# Revit family: NLRS_27_GM_LIB_GVIP_MR
name_source: partatom
category: Generic Models
revit_build: Autodesk Revit 2017 (Build: 20190507_1515(x64)
units: mm (PartAtom-declared; Revit-internal decimal feet)

## family parameters
Can host rebar = No
Cut with Voids When Loaded = Yes
Part Type = Normal
Room Calculation Point = No
Round Connector Dimension = Use Diameter
Shared = No

## types (6) — shared parameters
01_kraal = No
02_Trim = Yes
03_druppel = Yes
Assembly Code = 27.16
Breedte_Plafond = 200 mm  [stored 0.656168 ft]
Description = GVIP Goot
IfcExportAs = IfcFlowsegment
Manufacturer = Meilof Riks bv
Model = GVIP
NLRS_C_Materiaal = RAL 9010
Type Image = <None>
URL = https://www.meilofriks.nl
Vorm_Goot_L = 01 : 2_←_Hoek_L
Vorm_Goot_L-R = 01 : 4_↔_Hoek_L-R
Vorm_Goot_R = 01 : 3_→_Hoek_R

## per-type parameters (varying)
| type | Breedte_goot | Breedte_goot_hoek | Diepte_bak | Hoogte_AK | Hoogte_VK | NLRS_C_Binnenbak | Set_Diepte_bak | set_Hoogte_AK |
| GVIP S310B | 310 mm  [stored 1.01706 ft] | 310 mm  [stored 1.01706 ft] | 76 mm  [stored 0.249344 ft] | 219 mm  [stored 0.718504 ft] | 193 mm  [stored 0.633202 ft] | RAL 7036 | 76 mm  [stored 0.249344 ft] | 219 mm  [stored 0.718504 ft] |
| GVIP S280B | 280 mm  [stored 0.918635 ft] | 280 mm  [stored 0.918635 ft] | 90 mm  [stored 0.295276 ft] | 210 mm | 182 mm | RAL 9010 | 90 mm  [stored 0.295276 ft] | 210 mm |
| GVIP S365B | 365 mm  [stored 1.19751 ft] | 365 mm  [stored 1.19751 ft] | 96 mm | 243 mm | 214 mm | RAL 9010 | 96 mm | 243 mm |
| GVIP S400B | 400 mm  [stored 1.31234 ft] | 400 mm  [stored 1.31234 ft] | 78 mm | 227 mm | 195 mm | RAL 9010 | 78 mm | 227 mm |
| GVIP S450B | 450 mm | 450 mm | 103 mm | 251 mm | 221 mm | RAL 9010 | 90 mm  [stored 0.295276 ft] | 251 mm |
| GVIP S500B | 500 mm  [stored 1.64042 ft] | 500 mm  [stored 1.64042 ft] | 78 mm | 226 mm | 196 mm  [stored 0.643045 ft] | RAL 9010 | 78 mm | 226 mm |

note: [stored X ft] marks values corroborated as IEEE doubles in the binary element streams (Revit-internal decimal feet)

## geometry (parser evidence)
native form markers: Sweep x30
no freeform markers — native parametric forms only
